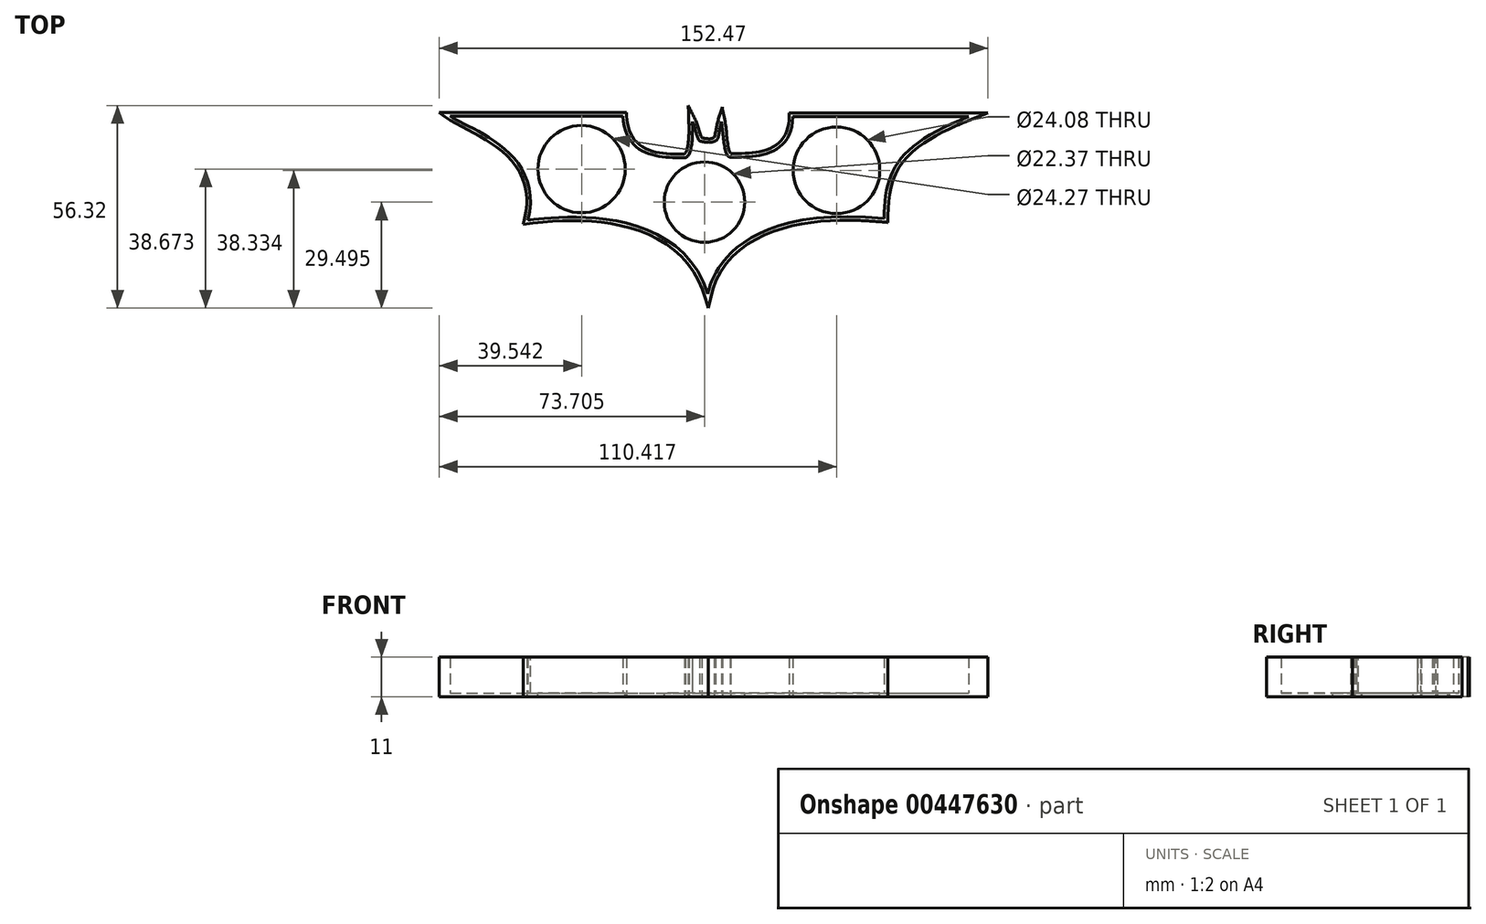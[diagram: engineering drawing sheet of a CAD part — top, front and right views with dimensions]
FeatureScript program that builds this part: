
annotation { "Feature Type Name" : "Feature", "Feature Type Description" : "" }
export const myFeature = defineFeature(function(context is Context, id is Id, definition is map)
    precondition{}
    {
        {
            var Q0;
            Q0=qCreatedBy(makeId("Top.planeOp"),FACE);
            var sketch = newSketch(context, id + "F0", { "sketchPlane" : qUnion([Q0])});
            skLineSegment(sketch, "E0", {"start": v(-72.47, 26.25) * mm, "end": v(-24.48, 26.25) * mm});
            skLineSegment(sketch, "E1", {"start": v(22.73, 26.1) * mm, "end": v(71.69, 26.1) * mm});
            skFitSpline(sketch, "E2", {"points": [v(-72.47, 26.25) * mm, v(-50.89, -2.74) * mm], "startDerivative": vector(14.5, -10.63) * mm, "endDerivative": vector(-14.5, -57.98) * mm});
            skFitSpline(sketch, "E3", {"points": [v(22.73, 26.1) * mm, v(5.34, 14.82) * mm], "startDerivative": vector(0, -35.75) * mm, "endDerivative": vector(-15.46, 0) * mm});
            skFitSpline(sketch, "E4", {"points": [v(-24.48, 26.25) * mm, v(-7.09, 14.65) * mm], "startDerivative": vector(1.93, -35.75) * mm, "endDerivative": vector(18.36, 0) * mm});
            skFitSpline(sketch, "E5", {"points": [v(-5.15, 24.64) * mm, v(-7.09, 14.65) * mm], "startDerivative": vector(0.49, -13.78) * mm, "endDerivative": vector(-5.15, -1.84) * mm});
            skFitSpline(sketch, "E6", {"points": [v(2.9, 24.64) * mm, v(5.34, 14.82) * mm], "startDerivative": vector(1.93, -9.98) * mm, "endDerivative": vector(5.72, -0.83) * mm});
            skFitSpline(sketch, "E7", {"points": [v(2.9, 24.64) * mm, v(1.23, 19.33) * mm], "startDerivative": vector(-1.67, -5.3) * mm, "endDerivative": vector(-2.85, 0) * mm});
            skFitSpline(sketch, "E8", {"points": [v(-3.12, 19.3) * mm, v(1.23, 19.33) * mm], "startDerivative": vector(5.55, -1.2) * mm, "endDerivative": vector(3.7, 2) * mm});
            skFitSpline(sketch, "E9", {"points": [v(-0.91, -23.23) * mm, v(48.18, -2.25) * mm], "startDerivative": vector(2.74, 12.78) * mm, "endDerivative": vector(126.44, -12.39) * mm});
            skFitSpline(sketch, "E10", {"points": [v(-50.89, -2.74) * mm, v(-0.91, -23.23) * mm], "startDerivative": vector(10.34, 1.26) * mm, "endDerivative": vector(25.14, -81.22) * mm});
            skFitSpline(sketch, "E11", {"points": [v(48.18, -2.25) * mm, v(71.69, 26.1) * mm], "startDerivative": vector(0, 39.58) * mm, "endDerivative": vector(59.88, 23.63) * mm});
            skFitSpline(sketch, "E12", {"points": [v(-5.15, 24.64) * mm, v(-3.12, 19.3) * mm], "startDerivative": vector(2.62, -5.16) * mm, "endDerivative": vector(2.52, -2.03) * mm});
            skSolve(sketch);
        }
        {
            var Q0;
            Q0=makeQuery(id+"F0.imprint","IMPRINT",FACE,{"disambiguationData":[TD([[makeQuery(id+"F0.imprint","IMPRINT",EDGE,{"derivedFrom":sQuery(id+"F0.wireOp",EDGE,"E0")}),-1.0]])]});
            extrude(context, id + "F1", {"entities" : qUnion([Q0]), "depth" : 10 * mm});
        }
        {
            var Q0;
            Q0=makeQuery(id+"F1.opExtrude","CAP_FACE",FACE,{"disambiguationData":[OSD([sQuery(id+"F0.wireOp",EDGE,"E0"),sQuery(id+"F0.wireOp",EDGE,"E1"),sQuery(id+"F0.wireOp",EDGE,"E2"),sQuery(id+"F0.wireOp",EDGE,"E3"),sQuery(id+"F0.wireOp",EDGE,"E4"),sQuery(id+"F0.wireOp",EDGE,"E5"),sQuery(id+"F0.wireOp",EDGE,"E6"),sQuery(id+"F0.wireOp",EDGE,"E7"),sQuery(id+"F0.wireOp",EDGE,"E8"),sQuery(id+"F0.wireOp",EDGE,"E9"),sQuery(id+"F0.wireOp",EDGE,"E10"),sQuery(id+"F0.wireOp",EDGE,"E11"),sQuery(id+"F0.wireOp",EDGE,"E12")])],"isStart":false});
            shell(context, id + "F2", {"entities" : qUnion([Q0]), "thickness" : 1 * mm, "oppositeDirection" : true});
        }
        {
            var Q0;
            Q0=makeQuery(id+"F0.imprint","IMPRINT",FACE,{"disambiguationData":[TD([[makeQuery(id+"F0.imprint","IMPRINT",EDGE,{"derivedFrom":sQuery(id+"F0.wireOp",EDGE,"E0")}),-1.0]])]});
            var sketch = newSketch(context, id + "F3", { "sketchPlane" : qUnion([Q0])});
            skCircle(sketch, "E13", {"center": v(-1.82, 2.32) * mm, "radius": 11.18 * mm});
            skCircle(sketch, "E14", {"center": v(34.9, 11.15) * mm, "radius": 12.04 * mm});
            skCircle(sketch, "E15", {"center": v(-35.98, 11.5) * mm, "radius": 12.13 * mm});
            skSolve(sketch);
        }
        {
            var Q0;
            Q0=makeQuery(id+"F3.imprint","IMPRINT",FACE,{"disambiguationData":[TD([[makeQuery(id+"F3.imprint","IMPRINT",EDGE,{"derivedFrom":sQuery(id+"F3.wireOp",EDGE,"E15")}),1.0]])]});
            var Q1;
            Q1=makeQuery(id+"F3.imprint","IMPRINT",FACE,{"disambiguationData":[TD([[makeQuery(id+"F3.imprint","IMPRINT",EDGE,{"derivedFrom":sQuery(id+"F3.wireOp",EDGE,"E13")}),1.0]])]});
            var Q2;
            Q2=makeQuery(id+"F3.imprint","IMPRINT",FACE,{"disambiguationData":[TD([[makeQuery(id+"F3.imprint","IMPRINT",EDGE,{"derivedFrom":sQuery(id+"F3.wireOp",EDGE,"E14")}),1.0]])]});
            extrude(context, id + "F4", {"entities" : qUnion([Q0, Q1, Q2]), "operationType" : NewBodyOperationType.REMOVE, "oppositeDirection" : true, "depth" : 10 * mm});
        }
    });
